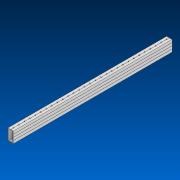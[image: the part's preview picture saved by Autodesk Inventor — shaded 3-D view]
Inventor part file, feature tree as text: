
AUTODESK INVENTOR PART (.ipt)
format: ipt  version: 2022.2 (Build 262287000, 287)  size: 513,024 bytes
history: native  units: in
note: dims shown in document units (in); Inventor stores cm internally (conversion verified against a paired STEP export)
features: other x30, extrude x1, pattern_linear x1, sketch x1
ambient origin geometry x8: Origin, YZ Plane, XZ Plane, XY Plane, X Axis, Y Axis, Z Axis, Center Point
bodies: Solid1 (feature_tree)
feature tree (33):
  extrude  "Extrusion1"  Depth=2.0in
  other  "Work Axis1"
  pattern_linear  "Rectangular Pattern1"  Spacing1=30.0in  [1 undecoded]
  sketch  "Sketch1"  dims[d0=1.0in d1=2.0in d2=30.0in d3=0.0in d4=11.4173in d6=1.0in]
  other  "Work Axis2"
  other  "Work Axis3"
  other  "Work Axis4"
  other  "Work Axis5"
  other  "Work Axis6"
  other  "Work Axis7"
  other  "Work Axis8"
  other  "Work Axis9"
  other  "Work Axis10"
  other  "Work Axis60"
  other  "Work Axis61"
  other  "Work Axis62"
  other  "Work Axis63"
  other  "Work Axis64"
  other  "Work Axis65"
  other  "Work Axis66"
  other  "Work Axis67"
  other  "Work Axis68"
  other  "Work Axis69"
  other  "Work Axis70"
  other  "Work Axis71"
  other  "Work Axis72"
  other  "Work Axis73"
  other  "Work Axis74"
  other  "Work Axis75"
  other  "Work Axis76"
  other  "Work Axis77"
  other  "Work Axis78"
  other  "Cut-Extrude2"
note: 1 required parameter value undecoded (feature->parameter linkage not recoverable at this tier; creation-order binding heuristic only, values carry confidence <= 0.55)
